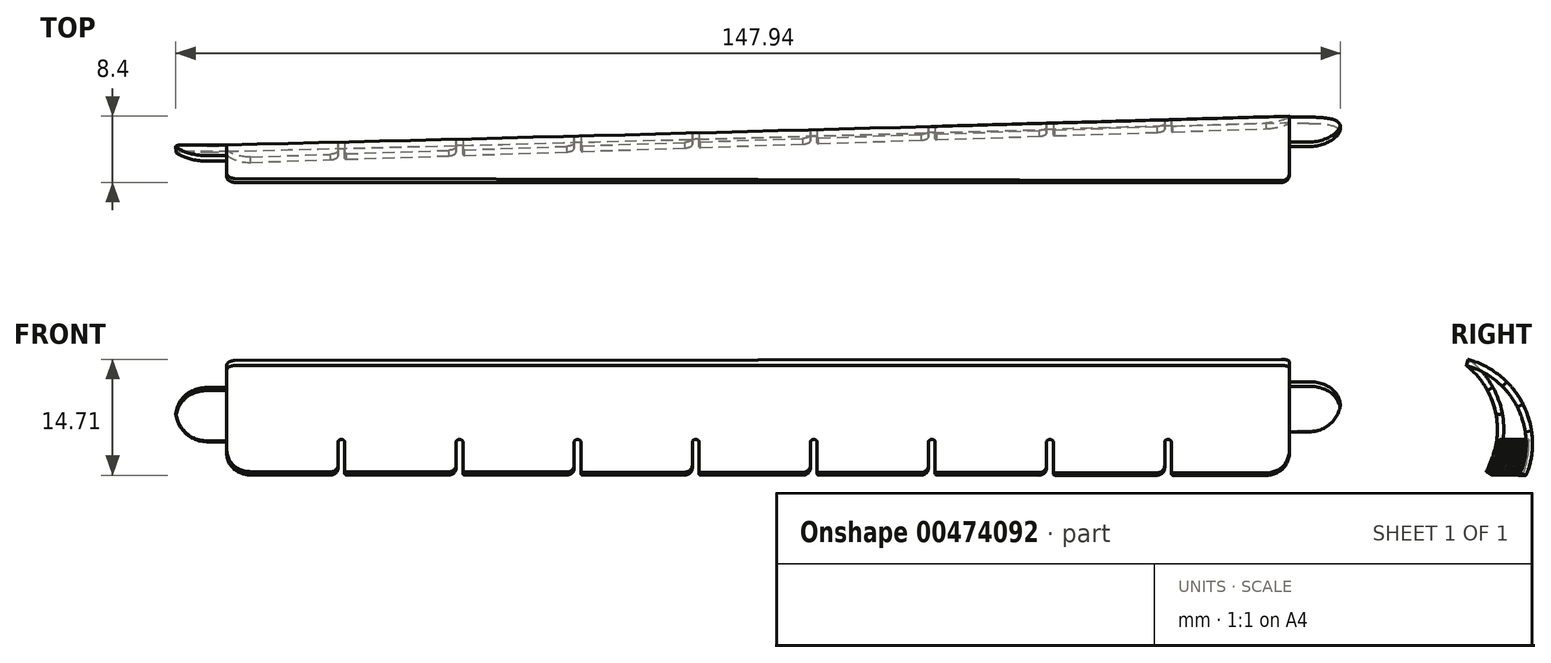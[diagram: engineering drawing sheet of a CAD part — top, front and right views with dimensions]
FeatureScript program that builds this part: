
annotation { "Feature Type Name" : "Feature", "Feature Type Description" : "" }
export const myFeature = defineFeature(function(context is Context, id is Id, definition is map)
    precondition{}
    {
        {
            var Q0;
            Q0=qCreatedBy(makeId("Right.planeOp"),FACE);
            var sketch = newSketch(context, id + "F0", { "sketchPlane" : qUnion([Q0])});
            skArc(sketch, "E0", {"start": v(2.44, -13.48) * mm, "mid": v(3.79, -6.28) * mm, "end": v(0, 0) * mm});
            skArc(sketch, "E1.0", {"start": v(3.12, -13.9) * mm, "mid": v(4.57, -6.13) * mm, "end": v(0.5, 0.63) * mm});
            skLineSegment(sketch, "E2", {"start": v(0, 0) * mm, "end": v(0.5, 0.63) * mm});
            skLineSegment(sketch, "E3", {"start": v(2.44, -13.48) * mm, "end": v(3.12, -13.9) * mm});
            skLineSegment(sketch, "E4", {"start": v(-6.35, -8.1) * mm, "end": v(0, 0) * mm, "construction": true});
            skSolve(sketch);
        }
        {
            var Q0;
            Q0=qCreatedBy(makeId("Right.planeOp"),FACE);
            cPlane(context, id + "F1", {"entities" : qUnion([Q0]), "cplaneType" : CPlaneType.OFFSET, "offset" : 135 * mm, "width" : 150 * mm, "height" : 150 * mm});
        }
        {
            var Q0;
            Q0=qCreatedBy(id+"F1.planeOp",FACE);
            var sketch = newSketch(context, id + "F2", { "sketchPlane" : qUnion([Q0])});
            skArc(sketch, "E5", {"start": v(6.9, -13.65) * mm, "mid": v(6.5, -5.29) * mm, "end": v(0, 0) * mm});
            skArc(sketch, "E6.0", {"start": v(7.65, -13.94) * mm, "mid": v(7.2, -4.93) * mm, "end": v(0.2, 0.77) * mm});
            skLineSegment(sketch, "E7", {"start": v(-2.7, -9.94) * mm, "end": v(0, 0) * mm, "construction": true});
            skLineSegment(sketch, "E8", {"start": v(0, 0) * mm, "end": v(0.2, 0.77) * mm});
            skLineSegment(sketch, "E9", {"start": v(-2.7, -9.94) * mm, "end": v(6.9, -13.65) * mm, "construction": true});
            skLineSegment(sketch, "E10", {"start": v(6.9, -13.65) * mm, "end": v(7.65, -13.94) * mm});
            skSolve(sketch);
        }
        {
            var Q0;
            Q0=makeQuery(id+"F0.imprint","IMPRINT",FACE,{"disambiguationData":[TD([[makeQuery(id+"F0.imprint","IMPRINT",EDGE,{"derivedFrom":sQuery(id+"F0.wireOp",EDGE,"E0")}),-1.0]])]});
            var Q1;
            Q1=makeQuery(id+"F2.imprint","IMPRINT",FACE,{"disambiguationData":[TD([[makeQuery(id+"F2.imprint","IMPRINT",EDGE,{"derivedFrom":sQuery(id+"F2.wireOp",EDGE,"E5")}),-1.0]])]});
            loft(context, id + "F3", {"sheetProfilesArray" : [{ "sheetProfileEntities" : qUnion([Q0]) }, { "sheetProfileEntities" : qUnion([Q1]) }]});
        }
        {
            var Q0;
            Q0=makeQuery(id+"F3.opLoft","CAP_FACE",FACE,{"disambiguationData":[OSD([makeQuery(id+"F0.imprint","IMPRINT",FACE,{"disambiguationData":[TD([[makeQuery(id+"F0.imprint","IMPRINT",EDGE,{"derivedFrom":sQuery(id+"F0.wireOp",EDGE,"E0")}),-1.0]])]})])],"isStart":true});
            var sketch = newSketch(context, id + "F4", { "sketchPlane" : qUnion([Q0])});
            skLineSegment(sketch, "E11.0", {"start": v(6.35, -8.1) * mm, "end": v(0, 0) * mm, "construction": true});
            skLineSegment(sketch, "E12", {"start": v(6.35, -8.1) * mm, "end": v(-4.57, -6.13) * mm, "construction": true});
            skLineSegment(sketch, "E13", {"start": v(6.35, -8.1) * mm, "end": v(-2.7, -3.17) * mm, "construction": true});
            skLineSegment(sketch, "E14", {"start": v(6.35, -8.1) * mm, "end": v(-3.85, -9.57) * mm, "construction": true});
            skArc(sketch, "E15.0", {"start": v(-3.85, -9.57) * mm, "mid": v(-3.79, -6.28) * mm, "end": v(-2.7, -3.17) * mm});
            skArc(sketch, "E16", {"start": v(-4.64, -9.68) * mm, "mid": v(-4.57, -6.13) * mm, "end": v(-3.4, -2.8) * mm});
            skLineSegment(sketch, "E17", {"start": v(-3.85, -9.57) * mm, "end": v(-4.64, -9.68) * mm});
            skLineSegment(sketch, "E18", {"start": v(-2.7, -3.17) * mm, "end": v(-3.4, -2.8) * mm});
            skPoint(sketch, "E19.orphan", {"position": v(-0.5, 0.63) * mm});
            skPoint(sketch, "E20.orphan", {"position": v(0, 0) * mm});
            skPoint(sketch, "E21.orphan", {"position": v(-2.44, -13.48) * mm});
            skFitSpline(sketch, "E22.0", {"points": [v(-3.12, -13.9) * mm, v(-3.82, -12.75) * mm, v(-4.8, -10.2) * mm, v(-4.82, -6.09) * mm, v(-3.37, -2.25) * mm, v(-1.55, -0.2) * mm, v(-0.5, 0.63) * mm], "construction": true});
            skSolve(sketch);
        }
        {
            var Q0;
            Q0=makeQuery(id+"F4.imprint","IMPRINT",FACE,{"disambiguationData":[TD([[makeQuery(id+"F4.imprint","IMPRINT",EDGE,{"derivedFrom":sQuery(id+"F4.wireOp",EDGE,"E15.0")}),1.0]])]});
            extrude(context, id + "F5", {"entities" : qUnion([Q0]), "operationType" : NewBodyOperationType.ADD, "depth" : 6.5 * mm});
        }
        {
            var Q0;
            Q0=makeQuery(id+"F3.opLoft","CAP_FACE",FACE,{"disambiguationData":[OSD([makeQuery(id+"F2.imprint","IMPRINT",FACE,{"disambiguationData":[TD([[makeQuery(id+"F2.imprint","IMPRINT",EDGE,{"derivedFrom":sQuery(id+"F2.wireOp",EDGE,"E5")}),-1.0]])]})])],"isStart":true});
            var sketch = newSketch(context, id + "F6", { "sketchPlane" : qUnion([Q0])});
            skLineSegment(sketch, "E23.0", {"start": v(-2.7, -9.94) * mm, "end": v(0, 0) * mm, "construction": true});
            skArc(sketch, "E24.0", {"start": v(7.65, -13.94) * mm, "mid": v(7.2, -4.93) * mm, "end": v(0.2, 0.77) * mm, "construction": true});
            skArc(sketch, "E25.0", {"start": v(6.9, -13.65) * mm, "mid": v(6.5, -5.29) * mm, "end": v(0, 0) * mm, "construction": true});
            skArc(sketch, "E26", {"start": v(8.28, -8.3) * mm, "mid": v(7.2, -4.93) * mm, "end": v(5.12, -2.06) * mm});
            skArc(sketch, "E27", {"start": v(7.49, -8.42) * mm, "mid": v(6.5, -5.29) * mm, "end": v(4.56, -2.63) * mm});
            skLineSegment(sketch, "E28", {"start": v(-2.7, -9.94) * mm, "end": v(7.49, -8.42) * mm, "construction": true});
            skLineSegment(sketch, "E29", {"start": v(7.49, -8.42) * mm, "end": v(8.28, -8.3) * mm});
            skLineSegment(sketch, "E30", {"start": v(-2.7, -9.94) * mm, "end": v(6.5, -5.29) * mm, "construction": true});
            skLineSegment(sketch, "E31", {"start": v(6.5, -5.29) * mm, "end": v(7.2, -4.93) * mm, "construction": true});
            skLineSegment(sketch, "E32", {"start": v(-2.7, -9.94) * mm, "end": v(4.56, -2.63) * mm, "construction": true});
            skLineSegment(sketch, "E33", {"start": v(4.56, -2.63) * mm, "end": v(5.12, -2.06) * mm});
            skSolve(sketch);
        }
        {
            var Q0;
            Q0=makeQuery(id+"F6.imprint","IMPRINT",FACE,{"disambiguationData":[TD([[makeQuery(id+"F6.imprint","IMPRINT",EDGE,{"derivedFrom":sQuery(id+"F6.wireOp",EDGE,"E26")}),1.0]])]});
            extrude(context, id + "F7", {"entities" : qUnion([Q0]), "operationType" : NewBodyOperationType.ADD, "depth" : 6.5 * mm});
        }
        {
            var Q0;
            Q0=makeQuery(id+"F7.opExtrude","CAP_EDGE",EDGE,{"disambiguationData":[OSD([sQuery(id+"F6.wireOp",EDGE,"E33")])],"isStart":false});
            var Q1;
            Q1=makeQuery(id+"F7.opExtrude","CAP_EDGE",EDGE,{"disambiguationData":[OSD([sQuery(id+"F6.wireOp",EDGE,"E29")])],"isStart":false});
            var Q2;
            Q2=makeQuery(id+"F5.opExtrude","CAP_EDGE",EDGE,{"disambiguationData":[OSD([sQuery(id+"F4.wireOp",EDGE,"E18")])],"isStart":false});
            var Q3;
            Q3=makeQuery(id+"F5.opExtrude","CAP_EDGE",EDGE,{"disambiguationData":[OSD([sQuery(id+"F4.wireOp",EDGE,"E17")])],"isStart":false});
            fillet(context, id + "F8", {"entities" : qUnion([Q0, Q1, Q2, Q3]), "radius" : 4 * mm, "tangentPropagation" : true, "allowEdgeOverflow" : false});
        }
        {
            var Q0;
            Q0=makeQuery(id+"F3.opLoft","MID_CAP_EDGE",EDGE,{"disambiguationData":[OSD([sQuery(id+"F0.wireOp",EDGE,"E0"),sQuery(id+"F0.wireOp",EDGE,"E1.0"),sQuery(id+"F0.wireOp",EDGE,"E2")])],"capPos":0.0});
            var Q1;
            Q1=makeQuery(id+"F3.opLoft","MID_CAP_EDGE",EDGE,{"disambiguationData":[OSD([sQuery(id+"F2.wireOp",EDGE,"E5"),sQuery(id+"F2.wireOp",EDGE,"E6.0"),sQuery(id+"F2.wireOp",EDGE,"E8")])],"capPos":1.0});
            fillet(context, id + "F9", {"entities" : qUnion([Q0, Q1]), "radius" : 1 * mm, "tangentPropagation" : true, "allowEdgeOverflow" : false});
        }
        {
            var Q0;
            Q0=makeQuery(id+"F3.opLoft","MID_CAP_EDGE",EDGE,{"disambiguationData":[OSD([sQuery(id+"F2.wireOp",EDGE,"E5"),sQuery(id+"F2.wireOp",EDGE,"E6.0"),sQuery(id+"F2.wireOp",EDGE,"E10")])],"capPos":1.0});
            var Q1;
            Q1=makeQuery(id+"F3.opLoft","MID_CAP_EDGE",EDGE,{"disambiguationData":[OSD([sQuery(id+"F0.wireOp",EDGE,"E0"),sQuery(id+"F0.wireOp",EDGE,"E1.0"),sQuery(id+"F0.wireOp",EDGE,"E3")])],"capPos":0.0});
            fillet(context, id + "F10", {"entities" : qUnion([Q0, Q1]), "radius" : 3 * mm, "tangentPropagation" : true, "allowEdgeOverflow" : false});
        }
        {
            var Q0;
            Q0=qCreatedBy(makeId("Front.planeOp"),FACE);
            var sketch = newSketch(context, id + "F11", { "sketchPlane" : qUnion([Q0])});
            skPoint(sketch, "E34.0", {"position": v(135, -11.03) * mm});
            skLineSegment(sketch, "E35.bottom", {"start": v(119.15, -9.63) * mm, "end": v(120, -9.63) * mm, "construction": true});
            skLineSegment(sketch, "E35.top", {"start": v(119.15, -13.63) * mm, "end": v(120, -13.63) * mm});
            skLineSegment(sketch, "E35.left", {"start": v(119.15, -9.63) * mm, "end": v(119.15, -13.63) * mm});
            skLineSegment(sketch, "E35.right", {"start": v(120, -9.63) * mm, "end": v(120, -13.63) * mm});
            skFitSpline(sketch, "E36.0", {"points": [v(3.05, -13.49) * mm, v(46.04, -13.54) * mm, v(89.04, -13.6) * mm, v(132.03, -13.65) * mm], "construction": true});
            skArc(sketch, "E37", {"start": v(120, -9.63) * mm, "mid": v(119.58, -9.4) * mm, "end": v(119.15, -9.63) * mm});
            skLineSegment(sketch, "E38", {"start": v(119.15, -13.63) * mm, "end": v(119.15, -14.63) * mm});
            skLineSegment(sketch, "E39", {"start": v(119.15, -14.63) * mm, "end": v(120, -14.63) * mm});
            skLineSegment(sketch, "E40", {"start": v(120, -14.63) * mm, "end": v(120, -13.63) * mm});
            skLineSegment(sketch, "E41.1.0.0", {"start": v(105, -9.63) * mm, "end": v(105, -13.63) * mm});
            skArc(sketch, "E41.1.0.1", {"start": v(105, -9.63) * mm, "mid": v(104.58, -9.4) * mm, "end": v(104.15, -9.63) * mm});
            skLineSegment(sketch, "E41.1.0.2", {"start": v(104.15, -13.63) * mm, "end": v(104.15, -14.63) * mm});
            skLineSegment(sketch, "E41.1.0.3", {"start": v(104.15, -14.63) * mm, "end": v(105, -14.63) * mm});
            skLineSegment(sketch, "E41.1.0.4", {"start": v(105, -14.63) * mm, "end": v(105, -13.63) * mm});
            skLineSegment(sketch, "E41.1.0.5", {"start": v(104.15, -9.63) * mm, "end": v(104.15, -13.63) * mm});
            skLineSegment(sketch, "E41.2.0.0", {"start": v(90, -9.63) * mm, "end": v(90, -13.63) * mm});
            skArc(sketch, "E41.2.0.1", {"start": v(90, -9.63) * mm, "mid": v(89.58, -9.4) * mm, "end": v(89.15, -9.63) * mm});
            skLineSegment(sketch, "E41.2.0.2", {"start": v(89.15, -13.63) * mm, "end": v(89.15, -14.63) * mm});
            skLineSegment(sketch, "E41.2.0.3", {"start": v(89.15, -14.63) * mm, "end": v(90, -14.63) * mm});
            skLineSegment(sketch, "E41.2.0.4", {"start": v(90, -14.63) * mm, "end": v(90, -13.63) * mm});
            skLineSegment(sketch, "E41.2.0.5", {"start": v(89.15, -9.63) * mm, "end": v(89.15, -13.63) * mm});
            skLineSegment(sketch, "E41.3.0.0", {"start": v(75, -9.63) * mm, "end": v(75, -13.63) * mm});
            skArc(sketch, "E41.3.0.1", {"start": v(75, -9.63) * mm, "mid": v(74.58, -9.4) * mm, "end": v(74.15, -9.63) * mm});
            skLineSegment(sketch, "E41.3.0.2", {"start": v(74.15, -13.63) * mm, "end": v(74.15, -14.63) * mm});
            skLineSegment(sketch, "E41.3.0.3", {"start": v(74.15, -14.63) * mm, "end": v(75, -14.63) * mm});
            skLineSegment(sketch, "E41.3.0.4", {"start": v(75, -14.63) * mm, "end": v(75, -13.63) * mm});
            skLineSegment(sketch, "E41.3.0.5", {"start": v(74.15, -9.63) * mm, "end": v(74.15, -13.63) * mm});
            skLineSegment(sketch, "E41.4.0.0", {"start": v(60, -9.63) * mm, "end": v(60, -13.63) * mm});
            skArc(sketch, "E41.4.0.1", {"start": v(60, -9.63) * mm, "mid": v(59.58, -9.4) * mm, "end": v(59.15, -9.63) * mm});
            skLineSegment(sketch, "E41.4.0.2", {"start": v(59.15, -13.63) * mm, "end": v(59.15, -14.63) * mm});
            skLineSegment(sketch, "E41.4.0.3", {"start": v(59.15, -14.63) * mm, "end": v(60, -14.63) * mm});
            skLineSegment(sketch, "E41.4.0.4", {"start": v(60, -14.63) * mm, "end": v(60, -13.63) * mm});
            skLineSegment(sketch, "E41.4.0.5", {"start": v(59.15, -9.63) * mm, "end": v(59.15, -13.63) * mm});
            skLineSegment(sketch, "E41.5.0.0", {"start": v(45, -9.63) * mm, "end": v(45, -13.63) * mm});
            skArc(sketch, "E41.5.0.1", {"start": v(45, -9.63) * mm, "mid": v(44.58, -9.4) * mm, "end": v(44.15, -9.63) * mm});
            skLineSegment(sketch, "E41.5.0.2", {"start": v(44.15, -13.63) * mm, "end": v(44.15, -14.63) * mm});
            skLineSegment(sketch, "E41.5.0.3", {"start": v(44.15, -14.63) * mm, "end": v(45, -14.63) * mm});
            skLineSegment(sketch, "E41.5.0.4", {"start": v(45, -14.63) * mm, "end": v(45, -13.63) * mm});
            skLineSegment(sketch, "E41.5.0.5", {"start": v(44.15, -9.63) * mm, "end": v(44.15, -13.63) * mm});
            skLineSegment(sketch, "E41.6.0.0", {"start": v(30, -9.63) * mm, "end": v(30, -13.63) * mm});
            skArc(sketch, "E41.6.0.1", {"start": v(30, -9.63) * mm, "mid": v(29.58, -9.4) * mm, "end": v(29.15, -9.63) * mm});
            skLineSegment(sketch, "E41.6.0.2", {"start": v(29.15, -13.63) * mm, "end": v(29.15, -14.63) * mm});
            skLineSegment(sketch, "E41.6.0.3", {"start": v(29.15, -14.63) * mm, "end": v(30, -14.63) * mm});
            skLineSegment(sketch, "E41.6.0.4", {"start": v(30, -14.63) * mm, "end": v(30, -13.63) * mm});
            skLineSegment(sketch, "E41.6.0.5", {"start": v(29.15, -9.63) * mm, "end": v(29.15, -13.63) * mm});
            skLineSegment(sketch, "E41.7.0.0", {"start": v(15, -9.63) * mm, "end": v(15, -13.63) * mm});
            skArc(sketch, "E41.7.0.1", {"start": v(15, -9.63) * mm, "mid": v(14.58, -9.4) * mm, "end": v(14.15, -9.63) * mm});
            skLineSegment(sketch, "E41.7.0.2", {"start": v(14.15, -13.63) * mm, "end": v(14.15, -14.63) * mm});
            skLineSegment(sketch, "E41.7.0.3", {"start": v(14.15, -14.63) * mm, "end": v(15, -14.63) * mm});
            skLineSegment(sketch, "E41.7.0.4", {"start": v(15, -14.63) * mm, "end": v(15, -13.63) * mm});
            skLineSegment(sketch, "E41.7.0.5", {"start": v(14.15, -9.63) * mm, "end": v(14.15, -13.63) * mm});
            skLineSegment(sketch, "E41.direction1", {"start": v(120, -13.63) * mm, "end": v(105, -13.63) * mm, "construction": true});
            skSolve(sketch);
        }
        {
            var Q0;
            Q0 = qSketchRegion(id + "F11", true);
            extrude(context, id + "F12", {"entities" : qUnion([Q0]), "operationType" : NewBodyOperationType.REMOVE, "oppositeDirection" : true, "depth" : 25 * mm});
        }
        {
            var Q0;
            Q0=makeQuery(id+"F12.boolean.opBoolean","INTERSECT",EDGE,{"derivedFrom":[makeQuery(id+"F3.opLoft","SWEPT_FACE",FACE,{"disambiguationData":[OSD([sQuery(id+"F0.wireOp",EDGE,"E0"),sQuery(id+"F0.wireOp",EDGE,"E1.0"),sQuery(id+"F0.wireOp",EDGE,"E3"),sQuery(id+"F2.wireOp",EDGE,"E5"),sQuery(id+"F2.wireOp",EDGE,"E6.0"),sQuery(id+"F2.wireOp",EDGE,"E10")])]}),makeQuery(id+"F12.opExtrude","SWEPT_FACE",FACE,{"disambiguationData":[OSD([sQuery(id+"F11.wireOp",EDGE,"E35.right"),sQuery(id+"F11.wireOp",EDGE,"E40")])]})]});
            var Q1;
            Q1=makeQuery(id+"F12.boolean.opBoolean","INTERSECT",EDGE,{"derivedFrom":[makeQuery(id+"F3.opLoft","SWEPT_FACE",FACE,{"disambiguationData":[OSD([sQuery(id+"F0.wireOp",EDGE,"E0"),sQuery(id+"F0.wireOp",EDGE,"E1.0"),sQuery(id+"F0.wireOp",EDGE,"E3"),sQuery(id+"F2.wireOp",EDGE,"E5"),sQuery(id+"F2.wireOp",EDGE,"E6.0"),sQuery(id+"F2.wireOp",EDGE,"E10")])]}),makeQuery(id+"F12.opExtrude","SWEPT_FACE",FACE,{"disambiguationData":[OSD([sQuery(id+"F11.wireOp",EDGE,"E41.1.0.0"),sQuery(id+"F11.wireOp",EDGE,"E41.1.0.4")])]})]});
            var Q2;
            Q2=makeQuery(id+"F12.boolean.opBoolean","INTERSECT",EDGE,{"derivedFrom":[makeQuery(id+"F3.opLoft","SWEPT_FACE",FACE,{"disambiguationData":[OSD([sQuery(id+"F0.wireOp",EDGE,"E0"),sQuery(id+"F0.wireOp",EDGE,"E1.0"),sQuery(id+"F0.wireOp",EDGE,"E3"),sQuery(id+"F2.wireOp",EDGE,"E5"),sQuery(id+"F2.wireOp",EDGE,"E6.0"),sQuery(id+"F2.wireOp",EDGE,"E10")])]}),makeQuery(id+"F12.opExtrude","SWEPT_FACE",FACE,{"disambiguationData":[OSD([sQuery(id+"F11.wireOp",EDGE,"E41.2.0.0"),sQuery(id+"F11.wireOp",EDGE,"E41.2.0.4")])]})]});
            var Q3;
            Q3=makeQuery(id+"F12.boolean.opBoolean","INTERSECT",EDGE,{"derivedFrom":[makeQuery(id+"F3.opLoft","SWEPT_FACE",FACE,{"disambiguationData":[OSD([sQuery(id+"F0.wireOp",EDGE,"E0"),sQuery(id+"F0.wireOp",EDGE,"E1.0"),sQuery(id+"F0.wireOp",EDGE,"E3"),sQuery(id+"F2.wireOp",EDGE,"E5"),sQuery(id+"F2.wireOp",EDGE,"E6.0"),sQuery(id+"F2.wireOp",EDGE,"E10")])]}),makeQuery(id+"F12.opExtrude","SWEPT_FACE",FACE,{"disambiguationData":[OSD([sQuery(id+"F11.wireOp",EDGE,"E41.3.0.0"),sQuery(id+"F11.wireOp",EDGE,"E41.3.0.4")])]})]});
            var Q4;
            Q4=makeQuery(id+"F12.boolean.opBoolean","INTERSECT",EDGE,{"derivedFrom":[makeQuery(id+"F3.opLoft","SWEPT_FACE",FACE,{"disambiguationData":[OSD([sQuery(id+"F0.wireOp",EDGE,"E0"),sQuery(id+"F0.wireOp",EDGE,"E1.0"),sQuery(id+"F0.wireOp",EDGE,"E3"),sQuery(id+"F2.wireOp",EDGE,"E5"),sQuery(id+"F2.wireOp",EDGE,"E6.0"),sQuery(id+"F2.wireOp",EDGE,"E10")])]}),makeQuery(id+"F12.opExtrude","SWEPT_FACE",FACE,{"disambiguationData":[OSD([sQuery(id+"F11.wireOp",EDGE,"E41.4.0.0"),sQuery(id+"F11.wireOp",EDGE,"E41.4.0.4")])]})]});
            var Q5;
            Q5=makeQuery(id+"F12.boolean.opBoolean","INTERSECT",EDGE,{"derivedFrom":[makeQuery(id+"F3.opLoft","SWEPT_FACE",FACE,{"disambiguationData":[OSD([sQuery(id+"F0.wireOp",EDGE,"E0"),sQuery(id+"F0.wireOp",EDGE,"E1.0"),sQuery(id+"F0.wireOp",EDGE,"E3"),sQuery(id+"F2.wireOp",EDGE,"E5"),sQuery(id+"F2.wireOp",EDGE,"E6.0"),sQuery(id+"F2.wireOp",EDGE,"E10")])]}),makeQuery(id+"F12.opExtrude","SWEPT_FACE",FACE,{"disambiguationData":[OSD([sQuery(id+"F11.wireOp",EDGE,"E41.5.0.0"),sQuery(id+"F11.wireOp",EDGE,"E41.5.0.4")])]})]});
            var Q6;
            Q6=makeQuery(id+"F12.boolean.opBoolean","INTERSECT",EDGE,{"derivedFrom":[makeQuery(id+"F3.opLoft","SWEPT_FACE",FACE,{"disambiguationData":[OSD([sQuery(id+"F0.wireOp",EDGE,"E0"),sQuery(id+"F0.wireOp",EDGE,"E1.0"),sQuery(id+"F0.wireOp",EDGE,"E3"),sQuery(id+"F2.wireOp",EDGE,"E5"),sQuery(id+"F2.wireOp",EDGE,"E6.0"),sQuery(id+"F2.wireOp",EDGE,"E10")])]}),makeQuery(id+"F12.opExtrude","SWEPT_FACE",FACE,{"disambiguationData":[OSD([sQuery(id+"F11.wireOp",EDGE,"E41.6.0.0"),sQuery(id+"F11.wireOp",EDGE,"E41.6.0.4")])]})]});
            var Q7;
            Q7=makeQuery(id+"F12.boolean.opBoolean","INTERSECT",EDGE,{"derivedFrom":[makeQuery(id+"F3.opLoft","SWEPT_FACE",FACE,{"disambiguationData":[OSD([sQuery(id+"F0.wireOp",EDGE,"E0"),sQuery(id+"F0.wireOp",EDGE,"E1.0"),sQuery(id+"F0.wireOp",EDGE,"E3"),sQuery(id+"F2.wireOp",EDGE,"E5"),sQuery(id+"F2.wireOp",EDGE,"E6.0"),sQuery(id+"F2.wireOp",EDGE,"E10")])]}),makeQuery(id+"F12.opExtrude","SWEPT_FACE",FACE,{"disambiguationData":[OSD([sQuery(id+"F11.wireOp",EDGE,"E41.7.0.0"),sQuery(id+"F11.wireOp",EDGE,"E41.7.0.4")])]})]});
            fillet(context, id + "F13", {"entities" : qUnion([Q0, Q1, Q2, Q3, Q4, Q5, Q6, Q7]), "radius" : 0.2 * mm, "tangentPropagation" : true, "allowEdgeOverflow" : false});
        }
        {
            var Q0;
            Q0=makeQuery(id+"F12.boolean.opBoolean","INTERSECT",EDGE,{"derivedFrom":[makeQuery(id+"F3.opLoft","SWEPT_FACE",FACE,{"disambiguationData":[OSD([sQuery(id+"F0.wireOp",EDGE,"E0"),sQuery(id+"F0.wireOp",EDGE,"E1.0"),sQuery(id+"F0.wireOp",EDGE,"E3"),sQuery(id+"F2.wireOp",EDGE,"E5"),sQuery(id+"F2.wireOp",EDGE,"E6.0"),sQuery(id+"F2.wireOp",EDGE,"E10")])]}),makeQuery(id+"F12.opExtrude","SWEPT_FACE",FACE,{"disambiguationData":[OSD([sQuery(id+"F11.wireOp",EDGE,"E41.7.0.2"),sQuery(id+"F11.wireOp",EDGE,"E41.7.0.5")])]})]});
            var Q1;
            Q1=makeQuery(id+"F12.boolean.opBoolean","INTERSECT",EDGE,{"derivedFrom":[makeQuery(id+"F3.opLoft","SWEPT_FACE",FACE,{"disambiguationData":[OSD([sQuery(id+"F0.wireOp",EDGE,"E0"),sQuery(id+"F0.wireOp",EDGE,"E1.0"),sQuery(id+"F0.wireOp",EDGE,"E3"),sQuery(id+"F2.wireOp",EDGE,"E5"),sQuery(id+"F2.wireOp",EDGE,"E6.0"),sQuery(id+"F2.wireOp",EDGE,"E10")])]}),makeQuery(id+"F12.opExtrude","SWEPT_FACE",FACE,{"disambiguationData":[OSD([sQuery(id+"F11.wireOp",EDGE,"E41.6.0.2"),sQuery(id+"F11.wireOp",EDGE,"E41.6.0.5")])]})]});
            var Q2;
            Q2=makeQuery(id+"F12.boolean.opBoolean","INTERSECT",EDGE,{"derivedFrom":[makeQuery(id+"F3.opLoft","SWEPT_FACE",FACE,{"disambiguationData":[OSD([sQuery(id+"F0.wireOp",EDGE,"E0"),sQuery(id+"F0.wireOp",EDGE,"E1.0"),sQuery(id+"F0.wireOp",EDGE,"E3"),sQuery(id+"F2.wireOp",EDGE,"E5"),sQuery(id+"F2.wireOp",EDGE,"E6.0"),sQuery(id+"F2.wireOp",EDGE,"E10")])]}),makeQuery(id+"F12.opExtrude","SWEPT_FACE",FACE,{"disambiguationData":[OSD([sQuery(id+"F11.wireOp",EDGE,"E41.5.0.2"),sQuery(id+"F11.wireOp",EDGE,"E41.5.0.5")])]})]});
            var Q3;
            Q3=makeQuery(id+"F12.boolean.opBoolean","INTERSECT",EDGE,{"derivedFrom":[makeQuery(id+"F3.opLoft","SWEPT_FACE",FACE,{"disambiguationData":[OSD([sQuery(id+"F0.wireOp",EDGE,"E0"),sQuery(id+"F0.wireOp",EDGE,"E1.0"),sQuery(id+"F0.wireOp",EDGE,"E3"),sQuery(id+"F2.wireOp",EDGE,"E5"),sQuery(id+"F2.wireOp",EDGE,"E6.0"),sQuery(id+"F2.wireOp",EDGE,"E10")])]}),makeQuery(id+"F12.opExtrude","SWEPT_FACE",FACE,{"disambiguationData":[OSD([sQuery(id+"F11.wireOp",EDGE,"E41.4.0.2"),sQuery(id+"F11.wireOp",EDGE,"E41.4.0.5")])]})]});
            var Q4;
            Q4=makeQuery(id+"F12.boolean.opBoolean","INTERSECT",EDGE,{"derivedFrom":[makeQuery(id+"F3.opLoft","SWEPT_FACE",FACE,{"disambiguationData":[OSD([sQuery(id+"F0.wireOp",EDGE,"E0"),sQuery(id+"F0.wireOp",EDGE,"E1.0"),sQuery(id+"F0.wireOp",EDGE,"E3"),sQuery(id+"F2.wireOp",EDGE,"E5"),sQuery(id+"F2.wireOp",EDGE,"E6.0"),sQuery(id+"F2.wireOp",EDGE,"E10")])]}),makeQuery(id+"F12.opExtrude","SWEPT_FACE",FACE,{"disambiguationData":[OSD([sQuery(id+"F11.wireOp",EDGE,"E41.3.0.2"),sQuery(id+"F11.wireOp",EDGE,"E41.3.0.5")])]})]});
            var Q5;
            Q5=makeQuery(id+"F12.boolean.opBoolean","INTERSECT",EDGE,{"derivedFrom":[makeQuery(id+"F3.opLoft","SWEPT_FACE",FACE,{"disambiguationData":[OSD([sQuery(id+"F0.wireOp",EDGE,"E0"),sQuery(id+"F0.wireOp",EDGE,"E1.0"),sQuery(id+"F0.wireOp",EDGE,"E3"),sQuery(id+"F2.wireOp",EDGE,"E5"),sQuery(id+"F2.wireOp",EDGE,"E6.0"),sQuery(id+"F2.wireOp",EDGE,"E10")])]}),makeQuery(id+"F12.opExtrude","SWEPT_FACE",FACE,{"disambiguationData":[OSD([sQuery(id+"F11.wireOp",EDGE,"E41.2.0.2"),sQuery(id+"F11.wireOp",EDGE,"E41.2.0.5")])]})]});
            var Q6;
            Q6=makeQuery(id+"F12.boolean.opBoolean","INTERSECT",EDGE,{"derivedFrom":[makeQuery(id+"F3.opLoft","SWEPT_FACE",FACE,{"disambiguationData":[OSD([sQuery(id+"F0.wireOp",EDGE,"E0"),sQuery(id+"F0.wireOp",EDGE,"E1.0"),sQuery(id+"F0.wireOp",EDGE,"E3"),sQuery(id+"F2.wireOp",EDGE,"E5"),sQuery(id+"F2.wireOp",EDGE,"E6.0"),sQuery(id+"F2.wireOp",EDGE,"E10")])]}),makeQuery(id+"F12.opExtrude","SWEPT_FACE",FACE,{"disambiguationData":[OSD([sQuery(id+"F11.wireOp",EDGE,"E41.1.0.2"),sQuery(id+"F11.wireOp",EDGE,"E41.1.0.5")])]})]});
            var Q7;
            Q7=makeQuery(id+"F12.boolean.opBoolean","INTERSECT",EDGE,{"derivedFrom":[makeQuery(id+"F3.opLoft","SWEPT_FACE",FACE,{"disambiguationData":[OSD([sQuery(id+"F0.wireOp",EDGE,"E0"),sQuery(id+"F0.wireOp",EDGE,"E1.0"),sQuery(id+"F0.wireOp",EDGE,"E3"),sQuery(id+"F2.wireOp",EDGE,"E5"),sQuery(id+"F2.wireOp",EDGE,"E6.0"),sQuery(id+"F2.wireOp",EDGE,"E10")])]}),makeQuery(id+"F12.opExtrude","SWEPT_FACE",FACE,{"disambiguationData":[OSD([sQuery(id+"F11.wireOp",EDGE,"E35.left"),sQuery(id+"F11.wireOp",EDGE,"E38")])]})]});
            fillet(context, id + "F14", {"entities" : qUnion([Q0, Q1, Q2, Q3, Q4, Q5, Q6, Q7]), "radius" : 1 * mm, "tangentPropagation" : true, "allowEdgeOverflow" : false});
        }
    });
